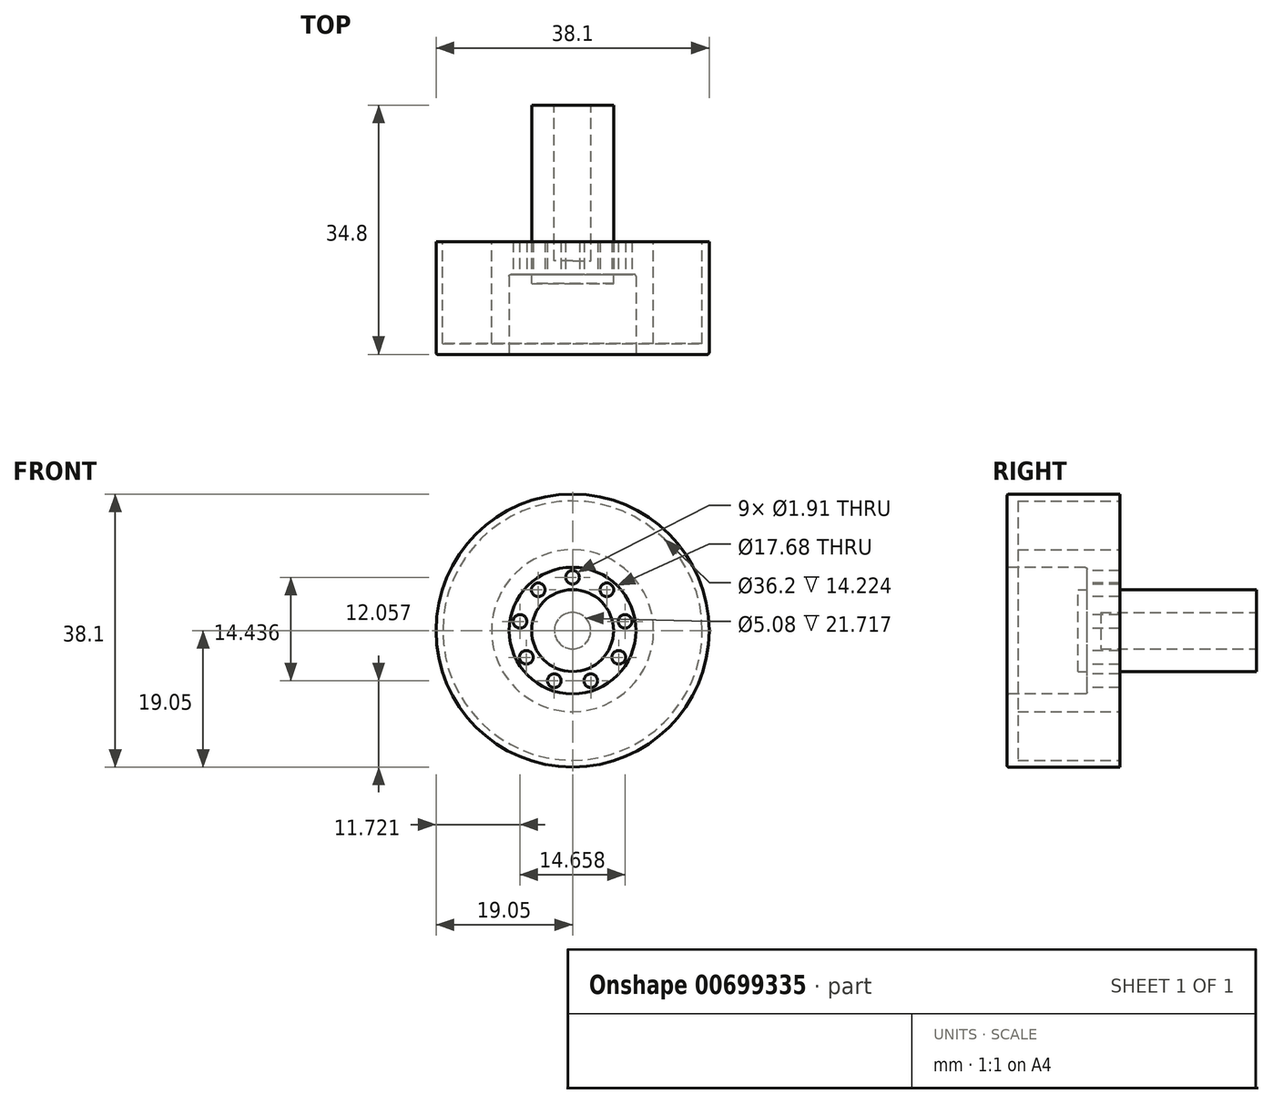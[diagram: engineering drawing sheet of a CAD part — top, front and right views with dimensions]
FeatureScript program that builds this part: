
annotation { "Feature Type Name" : "Feature", "Feature Type Description" : "" }
export const myFeature = defineFeature(function(context is Context, id is Id, definition is map)
    precondition{}
    {
        {
            var Q0;
            Q0=qCreatedBy(makeId("Front.planeOp"),FACE);
            var sketch = newSketch(context, id + "F0", { "sketchPlane" : qUnion([Q0])});
            skCircle(sketch, "E0", {"center": v(0, 0) * mm, "radius": 19.05 * mm});
            skSolve(sketch);
        }
        {
            var Q0;
            Q0 = qSketchRegion(id + "F0", true);
            extrude(context, id + "F1", {"entities" : qUnion([Q0]), "depth" : 15.75 * mm, "offsetDistance" : 25.4 * mm});
        }
        {
            var Q0;
            Q0=makeQuery(id+"F1.opExtrude","CAP_EDGE",EDGE,{"disambiguationData":[OSD([sQuery(id+"F0.wireOp",EDGE,"E0")])],"isStart":false});
            fillet(context, id + "F2", {"entities" : qUnion([Q0]), "radius" : 0.25 * mm, "tangentPropagation" : true, "allowEdgeOverflow" : false});
        }
        {
            var Q0;
            Q0=makeQuery(id+"F1.opExtrude","CAP_FACE",FACE,{"disambiguationData":[OSD([sQuery(id+"F0.wireOp",EDGE,"E0")])],"isStart":false});
            var sketch = newSketch(context, id + "F3", { "sketchPlane" : qUnion([Q0])});
            skCircle(sketch, "E1", {"center": v(0, 0) * mm, "radius": 8.84 * mm});
            skSolve(sketch);
        }
        {
            var Q0;
            Q0 = qSketchRegion(id + "F3", true);
            extrude(context, id + "F4", {"entities" : qUnion([Q0]), "operationType" : NewBodyOperationType.REMOVE, "oppositeDirection" : true, "depth" : 11.18 * mm, "offsetDistance" : 25.4 * mm});
        }
        {
            var Q0;
            Q0=makeQuery(id+"F4.boolean.opBoolean","COPY",EDGE,{"derivedFrom":makeQuery(id+"F4.opExtrude","CAP_EDGE",EDGE,{"disambiguationData":[OSD([sQuery(id+"F3.wireOp",EDGE,"E1")])],"isStart":true})});
            var Q1;
            Q1=makeQuery(id+"F4.boolean.opBoolean","COPY",FACE,{"derivedFrom":makeQuery(id+"F4.opExtrude","SWEPT_FACE",FACE,{"disambiguationData":[OSD([sQuery(id+"F3.wireOp",EDGE,"E1")])]})});
            fillet(context, id + "F5", {"entities" : qUnion([Q0, Q1]), "radius" : 0.25 * mm, "tangentPropagation" : true, "allowEdgeOverflow" : false});
        }
        {
            var Q0;
            Q0=makeQuery(id+"F4.boolean.opBoolean","COPY",FACE,{"derivedFrom":makeQuery(id+"F4.opExtrude","CAP_FACE",FACE,{"disambiguationData":[OSD([sQuery(id+"F3.wireOp",EDGE,"E1")])],"isStart":false})});
            var sketch = newSketch(context, id + "F6", { "sketchPlane" : qUnion([Q0])});
            skCircle(sketch, "E2", {"center": v(0, 7.44) * mm, "radius": 0.95 * mm});
            skCircle(sketch, "E3.1.0", {"center": v(6.45, -3.72) * mm, "radius": 0.95 * mm});
            skCircle(sketch, "E3.2.0", {"center": v(-6.45, -3.72) * mm, "radius": 0.95 * mm});
            skPoint(sketch, "E3.center", {"position": v(0, 0) * mm});
            skLineSegment(sketch, "E3.anchor1", {"start": v(0, 0) * mm, "end": v(0, 7.44) * mm, "construction": true});
            skLineSegment(sketch, "E3.anchor2", {"start": v(0, 0) * mm, "end": v(-6.45, -3.72) * mm, "construction": true});
            skCircle(sketch, "E4.1.0", {"center": v(-4.78, 5.7) * mm, "radius": 0.95 * mm});
            skCircle(sketch, "E4.1.1", {"center": v(-2.55, -7) * mm, "radius": 0.95 * mm});
            skCircle(sketch, "E4.1.2", {"center": v(7.33, 1.3) * mm, "radius": 0.95 * mm});
            skCircle(sketch, "E4.2.0", {"center": v(4.78, 5.7) * mm, "radius": 0.95 * mm});
            skCircle(sketch, "E4.2.1", {"center": v(-7.33, 1.3) * mm, "radius": 0.95 * mm});
            skCircle(sketch, "E4.2.2", {"center": v(2.55, -7) * mm, "radius": 0.95 * mm});
            skLineSegment(sketch, "E4.anchor2", {"start": v(0, 0) * mm, "end": v(4.78, 5.7) * mm, "construction": true});
            skSolve(sketch);
        }
        {
            var Q0;
            Q0=makeQuery(id+"F6.imprint","IMPRINT",FACE,{"disambiguationData":[TD([[makeQuery(id+"F6.imprint","IMPRINT",EDGE,{"derivedFrom":sQuery(id+"F6.wireOp",EDGE,"E2")}),1.0]])]});
            var Q1;
            Q1=makeQuery(id+"F6.imprint","IMPRINT",FACE,{"disambiguationData":[TD([[makeQuery(id+"F6.imprint","IMPRINT",EDGE,{"derivedFrom":sQuery(id+"F6.wireOp",EDGE,"E4.2.0")}),1.0]])]});
            var Q2;
            Q2=makeQuery(id+"F6.imprint","IMPRINT",FACE,{"disambiguationData":[TD([[makeQuery(id+"F6.imprint","IMPRINT",EDGE,{"derivedFrom":sQuery(id+"F6.wireOp",EDGE,"E4.1.2")}),1.0]])]});
            var Q3;
            Q3=makeQuery(id+"F6.imprint","IMPRINT",FACE,{"disambiguationData":[TD([[makeQuery(id+"F6.imprint","IMPRINT",EDGE,{"derivedFrom":sQuery(id+"F6.wireOp",EDGE,"E3.1.0")}),1.0]])]});
            var Q4;
            Q4=makeQuery(id+"F6.imprint","IMPRINT",FACE,{"disambiguationData":[TD([[makeQuery(id+"F6.imprint","IMPRINT",EDGE,{"derivedFrom":sQuery(id+"F6.wireOp",EDGE,"E4.2.2")}),1.0]])]});
            var Q5;
            Q5=makeQuery(id+"F6.imprint","IMPRINT",FACE,{"disambiguationData":[TD([[makeQuery(id+"F6.imprint","IMPRINT",EDGE,{"derivedFrom":sQuery(id+"F6.wireOp",EDGE,"E4.1.1")}),1.0]])]});
            var Q6;
            Q6=makeQuery(id+"F6.imprint","IMPRINT",FACE,{"disambiguationData":[TD([[makeQuery(id+"F6.imprint","IMPRINT",EDGE,{"derivedFrom":sQuery(id+"F6.wireOp",EDGE,"E3.2.0")}),1.0]])]});
            var Q7;
            Q7=makeQuery(id+"F6.imprint","IMPRINT",FACE,{"disambiguationData":[TD([[makeQuery(id+"F6.imprint","IMPRINT",EDGE,{"derivedFrom":sQuery(id+"F6.wireOp",EDGE,"E4.2.1")}),1.0]])]});
            var Q8;
            Q8=makeQuery(id+"F6.imprint","IMPRINT",FACE,{"disambiguationData":[TD([[makeQuery(id+"F6.imprint","IMPRINT",EDGE,{"derivedFrom":sQuery(id+"F6.wireOp",EDGE,"E4.1.0")}),1.0]])]});
            extrude(context, id + "F7", {"entities" : qUnion([Q0, Q1, Q2, Q3, Q4, Q5, Q6, Q7, Q8]), "operationType" : NewBodyOperationType.REMOVE, "oppositeDirection" : true, "depth" : 25.4 * mm, "offsetDistance" : 25.4 * mm});
        }
        {
            var Q0;
            Q0=makeQuery(id+"F4.boolean.opBoolean","COPY",FACE,{"derivedFrom":makeQuery(id+"F4.opExtrude","CAP_FACE",FACE,{"disambiguationData":[OSD([sQuery(id+"F3.wireOp",EDGE,"E1")])],"isStart":false})});
            var sketch = newSketch(context, id + "F8", { "sketchPlane" : qUnion([Q0])});
            skCircle(sketch, "E5", {"center": v(0, 0) * mm, "radius": 5.72 * mm});
            skSolve(sketch);
        }
        {
            var Q0;
            Q0=makeQuery(id+"F8.imprint","IMPRINT",FACE,{"disambiguationData":[TD([[makeQuery(id+"F8.imprint","IMPRINT",EDGE,{"derivedFrom":sQuery(id+"F8.wireOp",EDGE,"E5")}),1.0]])]});
            extrude(context, id + "F9", {"entities" : qUnion([Q0]), "operationType" : NewBodyOperationType.ADD, "depth" : 1.27 * mm, "offsetDistance" : 25.4 * mm});
        }
        {
            var Q0;
            Q0=makeQuery(id+"F1.opExtrude","CAP_FACE",FACE,{"disambiguationData":[OSD([sQuery(id+"F0.wireOp",EDGE,"E0")])],"isStart":true});
            var sketch = newSketch(context, id + "F10", { "sketchPlane" : qUnion([Q0])});
            skCircle(sketch, "E6", {"center": v(0, 0) * mm, "radius": 5.72 * mm});
            skSolve(sketch);
        }
        {
            var Q0;
            Q0=makeQuery(id+"F1.opExtrude","CAP_FACE",FACE,{"disambiguationData":[OSD([sQuery(id+"F0.wireOp",EDGE,"E0")])],"isStart":true});
            var sketch = newSketch(context, id + "F11", { "sketchPlane" : qUnion([Q0])});
            skCircle(sketch, "E7", {"center": v(0, 0) * mm, "radius": 11.3 * mm});
            skCircle(sketch, "E8", {"center": v(0, 0) * mm, "radius": 18.1 * mm});
            skSolve(sketch);
        }
        {
            var Q0;
            Q0=makeQuery(id+"F11.imprint","IMPRINT",FACE,{"disambiguationData":[TD([[makeQuery(id+"F11.imprint","IMPRINT",EDGE,{"derivedFrom":sQuery(id+"F11.wireOp",EDGE,"E7")}),-1.0]])]});
            extrude(context, id + "F12", {"entities" : qUnion([Q0]), "operationType" : NewBodyOperationType.REMOVE, "oppositeDirection" : true, "depth" : 14.22 * mm, "offsetDistance" : 25.4 * mm});
        }
        {
            var Q0;
            Q0=makeQuery(id+"F10.imprint","IMPRINT",FACE,{"disambiguationData":[TD([[makeQuery(id+"F10.imprint","IMPRINT",EDGE,{"derivedFrom":sQuery(id+"F10.wireOp",EDGE,"E6")}),1.0]])]});
            extrude(context, id + "F13", {"entities" : qUnion([Q0]), "operationType" : NewBodyOperationType.ADD, "depth" : 19.05 * mm, "offsetDistance" : 25.4 * mm});
        }
        {
            var Q0;
            Q0=makeQuery(id+"F13.opExtrude","CAP_FACE",FACE,{"disambiguationData":[OSD([sQuery(id+"F10.wireOp",EDGE,"E6")])],"isStart":false});
            shell(context, id + "F14", {"entities" : qUnion([Q0]), "thickness" : 3.17 * mm});
        }
    });
